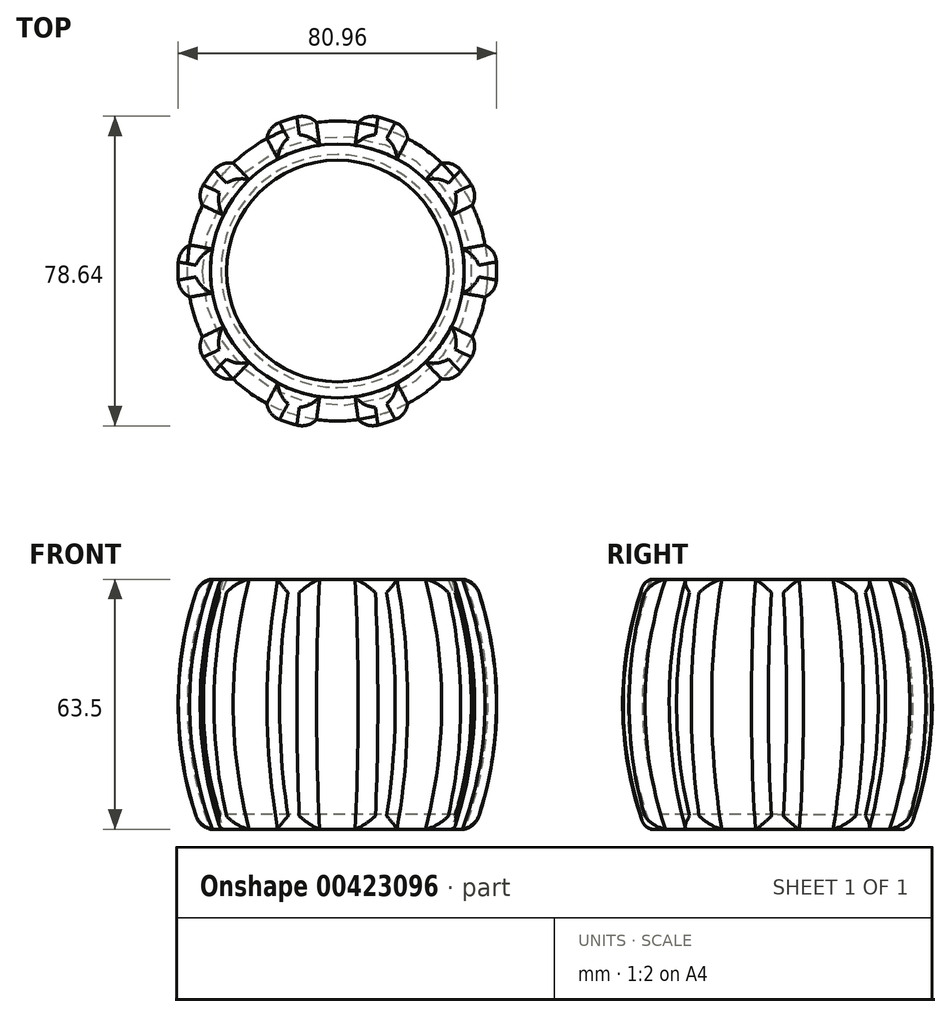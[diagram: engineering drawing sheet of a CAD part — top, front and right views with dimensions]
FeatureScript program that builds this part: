
annotation { "Feature Type Name" : "Feature", "Feature Type Description" : "" }
export const myFeature = defineFeature(function(context is Context, id is Id, definition is map)
    precondition{}
    {
        {
            var Q0;
            Q0=qCreatedBy(makeId("Front.planeOp"),FACE);
            var sketch = newSketch(context, id + "F0", { "sketchPlane" : qUnion([Q0])});
            skLineSegment(sketch, "E0", {"start": v(0, 0) * mm, "end": v(32.24, 0) * mm});
            skArc(sketch, "E1", {"start": v(32.24, 0) * mm, "mid": v(38.1, 31.75) * mm, "end": v(32.24, 63.5) * mm});
            skLineSegment(sketch, "E2", {"start": v(32.24, 63.5) * mm, "end": v(0, 63.5) * mm});
            skLineSegment(sketch, "E3", {"start": v(0, 63.5) * mm, "end": v(0, 0) * mm});
            skSolve(sketch);
        }
        {
            var Q0;
            Q0 = qSketchRegion(id + "F0", true);
            var Q1;
            Q1=sQuery(id+"F0.wireOp",EDGE,"E3");
            revolve(context, id + "F1", {"entities" : qUnion([Q0]), "axis" : qUnion([Q1]), "revolveType" : RevolveType.FULL});
        }
        {
            var Q0;
            Q0=makeQuery(id+"F1.opRevolve","SWEPT_FACE",FACE,{"disambiguationData":[OSD([sQuery(id+"F0.wireOp",EDGE,"E2")])]});
            shell(context, id + "F2", {"entities" : qUnion([Q0]), "thickness" : 3.8 * mm});
        }
        {
            var Q0;
            Q0=qCreatedBy(makeId("Front.planeOp"),FACE);
            var sketch = newSketch(context, id + "F3", { "sketchPlane" : qUnion([Q0])});
            skLineSegment(sketch, "E4", {"start": v(-32.24, 63.5) * mm, "end": v(-34.78, 63.5) * mm});
            skArc(sketch, "E5", {"start": v(-34.78, 63.5) * mm, "mid": v(-40.48, 31.75) * mm, "end": v(-34.78, 0) * mm});
            skArc(sketch, "E6", {"start": v(-32.24, 63.5) * mm, "mid": v(-38.1, 31.75) * mm, "end": v(-32.24, 0) * mm});
            skLineSegment(sketch, "E7", {"start": v(-34.78, 0) * mm, "end": v(-32.24, 0) * mm});
            skLineSegment(sketch, "E8", {"start": v(0, 0) * mm, "end": v(0, 69.7) * mm, "construction": true});
            skSolve(sketch);
        }
        {
            var Q0;
            Q0 = qSketchRegion(id + "F3", true);
            var Q1;
            Q1=sQuery(id+"F3.wireOp",EDGE,"E8");
            revolve(context, id + "F4", {"entities" : qUnion([Q0]), "axis" : qUnion([Q1]), "revolveType" : RevolveType.TWO_DIRECTIONS, "angle" : 10 * degree, "angleBack" : 350 * degree});
        }
        {
            var Q0;
            Q0=makeQuery(id+"F4.opRevolve","CAP_EDGE",EDGE,{"disambiguationData":[OSD([sQuery(id+"F3.wireOp",EDGE,"E5")])],"isStart":true});
            var Q1;
            Q1=makeQuery(id+"F4.opRevolve","SWEPT_EDGE",EDGE,{"disambiguationData":[OSD([sQuery(id+"F3.wireOp",EDGE,"E4"),sQuery(id+"F3.wireOp",EDGE,"E5")])]});
            var Q2;
            Q2=makeQuery(id+"F4.opRevolve","CAP_EDGE",EDGE,{"disambiguationData":[OSD([sQuery(id+"F3.wireOp",EDGE,"E5")])],"isStart":false});
            var Q3;
            Q3=makeQuery(id+"F4.opRevolve","SWEPT_EDGE",EDGE,{"disambiguationData":[OSD([sQuery(id+"F3.wireOp",EDGE,"E5"),sQuery(id+"F3.wireOp",EDGE,"E7")])]});
            fillet(context, id + "F5", {"entities" : qUnion([Q0, Q1, Q2, Q3]), "radius" : 5.08 * mm, "tangentPropagation" : true, "allowEdgeOverflow" : false});
        }
        {
            var Q0;
            Q0=makeQuery(id+"F4.opRevolve","SWEPT_BODY",BODY,{"disambiguationData":[OSD([sQuery(id+"F3.wireOp",EDGE,"E4"),sQuery(id+"F3.wireOp",EDGE,"E5"),sQuery(id+"F3.wireOp",EDGE,"E6"),sQuery(id+"F3.wireOp",EDGE,"E7")])]});
            var Q1;
            Q1=makeQuery(id+"F1.opRevolve","SWEPT_EDGE",EDGE,{"disambiguationData":[OSD([sQuery(id+"F0.wireOp",EDGE,"E1"),sQuery(id+"F0.wireOp",EDGE,"E2")])]});
            circularPattern(context, id + "F6", {"entities" : qUnion([Q0]), "axis" : qUnion([Q1]), "angle" : 360 * degree, "instanceCount" : 10, "equalSpace" : true});
        }
    });
